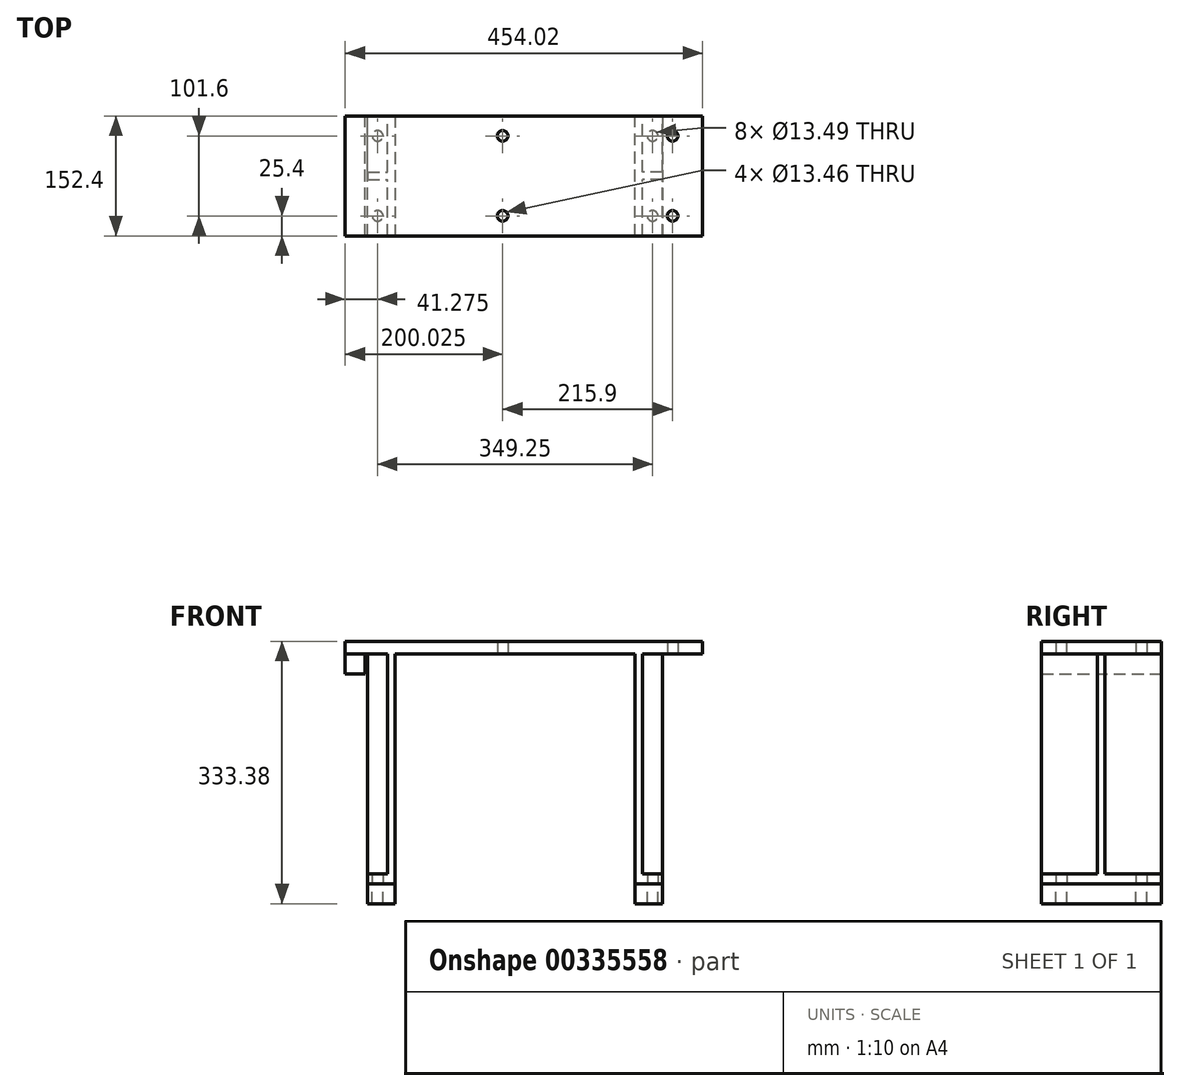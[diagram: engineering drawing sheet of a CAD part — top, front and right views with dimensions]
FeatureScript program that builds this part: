
annotation { "Feature Type Name" : "Feature", "Feature Type Description" : "" }
export const myFeature = defineFeature(function(context is Context, id is Id, definition is map)
    precondition{}
    {
        {
            var Q0;
            Q0=qCreatedBy(makeId("Top.planeOp"),FACE);
            var sketch = newSketch(context, id + "F0", { "sketchPlane" : qUnion([Q0])});
            skLineSegment(sketch, "E0", {"start": v(0, 170.24) * mm, "end": v(0, -171.77) * mm, "construction": true});
            skLineSegment(sketch, "E1", {"start": v(-339.85, 0) * mm, "end": v(353.8, 0) * mm, "construction": true});
            skLineSegment(sketch, "E2.0", {"start": v(-215.9, 170.24) * mm, "end": v(-215.9, -171.77) * mm, "construction": true});
            skLineSegment(sketch, "E3.0", {"start": v(-15.87, 170.24) * mm, "end": v(-15.87, -171.77) * mm, "construction": true});
            skLineSegment(sketch, "E4.0", {"start": v(-339.85, -76.2) * mm, "end": v(353.8, -76.2) * mm, "construction": true});
            skLineSegment(sketch, "E5.bottom", {"start": v(-215.9, -76.2) * mm, "end": v(238.13, -76.2) * mm});
            skLineSegment(sketch, "E5.top", {"start": v(-215.9, 76.2) * mm, "end": v(238.13, 76.2) * mm});
            skLineSegment(sketch, "E5.left", {"start": v(-215.9, -76.2) * mm, "end": v(-215.9, 76.2) * mm});
            skLineSegment(sketch, "E5.right", {"start": v(238.13, -76.2) * mm, "end": v(238.13, 76.2) * mm});
            skLineSegment(sketch, "E6.0", {"start": v(200.03, 170.24) * mm, "end": v(200.03, -171.77) * mm, "construction": true});
            skLineSegment(sketch, "E7.0", {"start": v(-339.85, -50.8) * mm, "end": v(353.8, -50.8) * mm, "construction": true});
            skPoint(sketch, "E8", {"position": v(-15.87, -50.8) * mm});
            skPoint(sketch, "E9", {"position": v(200.03, -50.8) * mm});
            skPoint(sketch, "E10.MirrorP", {"position": v(-15.87, 50.8) * mm});
            skPoint(sketch, "E11.MirrorP", {"position": v(200.03, 50.8) * mm});
            skCircle(sketch, "E12", {"center": v(-15.87, 50.8) * mm, "radius": 6.73 * mm});
            skCircle(sketch, "E13", {"center": v(200.03, 50.8) * mm, "radius": 6.73 * mm});
            skCircle(sketch, "E14", {"center": v(200.03, -50.8) * mm, "radius": 6.73 * mm});
            skCircle(sketch, "E15", {"center": v(-15.87, -50.8) * mm, "radius": 6.73 * mm});
            skSolve(sketch);
        }
        {
            var Q0;
            Q0 = qSketchRegion(id + "F0", true);
            extrude(context, id + "F1", {"entities" : qUnion([Q0]), "depth" : 15.88 * mm});
        }
        {
            var Q0;
            Q0=makeQuery(id+"F1.opExtrude","CAP_FACE",FACE,{"disambiguationData":[OSD([sQuery(id+"F0.wireOp",EDGE,"E5.bottom"),sQuery(id+"F0.wireOp",EDGE,"E5.top"),sQuery(id+"F0.wireOp",EDGE,"E5.left"),sQuery(id+"F0.wireOp",EDGE,"E5.right"),sQuery(id+"F0.wireOp",EDGE,"E12"),sQuery(id+"F0.wireOp",EDGE,"E13"),sQuery(id+"F0.wireOp",EDGE,"E14"),sQuery(id+"F0.wireOp",EDGE,"E15")])],"isStart":true});
            var sketch = newSketch(context, id + "F2", { "sketchPlane" : qUnion([Q0])});
            skLineSegment(sketch, "E16.bottom", {"start": v(-215.9, 76.2) * mm, "end": v(-190.5, 76.2) * mm});
            skLineSegment(sketch, "E16.top", {"start": v(-215.9, -76.2) * mm, "end": v(-190.5, -76.2) * mm});
            skLineSegment(sketch, "E16.left", {"start": v(-215.9, 76.2) * mm, "end": v(-215.9, -76.2) * mm});
            skLineSegment(sketch, "E16.right", {"start": v(-190.5, 76.2) * mm, "end": v(-190.5, -76.2) * mm});
            skSolve(sketch);
        }
        {
            var Q0;
            Q0=makeQuery(id+"F2.imprint","IMPRINT",FACE,{"disambiguationData":[TD([[makeQuery(id+"F2.imprint","IMPRINT",EDGE,{"derivedFrom":sQuery(id+"F2.wireOp",EDGE,"E16.bottom")}),-1.0]])]});
            extrude(context, id + "F3", {"entities" : qUnion([Q0]), "depth" : 25.4 * mm});
        }
        {
            var Q0;
            Q0=makeQuery(id+"F1.opExtrude","CAP_FACE",FACE,{"disambiguationData":[OSD([sQuery(id+"F0.wireOp",EDGE,"E5.bottom"),sQuery(id+"F0.wireOp",EDGE,"E5.top"),sQuery(id+"F0.wireOp",EDGE,"E5.left"),sQuery(id+"F0.wireOp",EDGE,"E5.right"),sQuery(id+"F0.wireOp",EDGE,"E12"),sQuery(id+"F0.wireOp",EDGE,"E13"),sQuery(id+"F0.wireOp",EDGE,"E14"),sQuery(id+"F0.wireOp",EDGE,"E15")])],"isStart":true});
            cPlane(context, id + "F4", {"entities" : qUnion([Q0]), "cplaneType" : CPlaneType.OFFSET, "offset" : 292.1 * mm, "width" : 152.4 * mm, "height" : 152.4 * mm});
        }
        {
            var Q0;
            Q0=qCreatedBy(makeId("Right.planeOp"),FACE);
            cPlane(context, id + "F5", {"entities" : qUnion([Q0]), "cplaneType" : CPlaneType.OFFSET, "offset" : 152.4 * mm, "width" : 152.4 * mm, "height" : 152.4 * mm});
        }
        {
            var Q0;
            Q0=qCreatedBy(id+"F5.planeOp",FACE);
            var sketch = newSketch(context, id + "F6", { "sketchPlane" : qUnion([Q0])});
            skLineSegment(sketch, "E17.0", {"start": v(-76.2, -25.4) * mm, "end": v(76.2, -25.4) * mm, "construction": true});
            skLineSegment(sketch, "E18.0", {"start": v(-76.2, 0) * mm, "end": v(76.2, 0) * mm, "construction": true});
            skLineSegment(sketch, "E19.bottom", {"start": v(76.2, 0) * mm, "end": v(-76.2, 0) * mm});
            skLineSegment(sketch, "E19.top", {"start": v(76.2, -292.1) * mm, "end": v(-76.2, -292.1) * mm});
            skLineSegment(sketch, "E19.left", {"start": v(76.2, 0) * mm, "end": v(76.2, -292.1) * mm});
            skLineSegment(sketch, "E19.right", {"start": v(-76.2, 0) * mm, "end": v(-76.2, -292.1) * mm});
            skSolve(sketch);
        }
        {
            var Q0;
            Q0=makeQuery(id+"F6.imprint","IMPRINT",FACE,{"disambiguationData":[TD([[makeQuery(id+"F6.imprint","IMPRINT",EDGE,{"derivedFrom":sQuery(id+"F6.wireOp",EDGE,"E19.bottom")}),1.0]])]});
            extrude(context, id + "F7", {"entities" : qUnion([Q0]), "depth" : 9.52 * mm});
        }
        {
            var Q0;
            Q0=qCreatedBy(id+"F4.planeOp",FACE);
            var sketch = newSketch(context, id + "F8", { "sketchPlane" : qUnion([Q0])});
            skLineSegment(sketch, "E20.0", {"start": v(161.93, -76.2) * mm, "end": v(161.93, 76.2) * mm, "construction": true});
            skLineSegment(sketch, "E21.0", {"start": v(187.33, -76.2) * mm, "end": v(187.33, 76.2) * mm, "construction": true});
            skLineSegment(sketch, "E22.0", {"start": v(152.4, -76.2) * mm, "end": v(152.4, 76.2) * mm, "construction": true});
            skLineSegment(sketch, "E23.bottom", {"start": v(152.4, 76.2) * mm, "end": v(187.33, 76.2) * mm});
            skLineSegment(sketch, "E23.top", {"start": v(152.4, -76.2) * mm, "end": v(187.33, -76.2) * mm});
            skLineSegment(sketch, "E23.left", {"start": v(152.4, 76.2) * mm, "end": v(152.4, -76.2) * mm});
            skLineSegment(sketch, "E23.right", {"start": v(187.33, 76.2) * mm, "end": v(187.33, -76.2) * mm});
            skSolve(sketch);
        }
        {
            var Q0;
            Q0 = qSketchRegion(id + "F8", true);
            extrude(context, id + "F9", {"entities" : qUnion([Q0]), "operationType" : NewBodyOperationType.ADD, "oppositeDirection" : true, "depth" : 12.7 * mm});
        }
        {
            var Q0;
            Q0=makeQuery(id+"F9.boolean.opBoolean","MERGE",FACE,{"derivedFrom":[makeQuery(id+"F7.opExtrude","SWEPT_FACE",FACE,{"disambiguationData":[OSD([sQuery(id+"F6.wireOp",EDGE,"E19.top")])]}),makeQuery(id+"F9.opExtrude","CAP_FACE",FACE,{"disambiguationData":[OSD([sQuery(id+"F8.wireOp",EDGE,"E23.bottom"),sQuery(id+"F8.wireOp",EDGE,"E23.top"),sQuery(id+"F8.wireOp",EDGE,"E23.left"),sQuery(id+"F8.wireOp",EDGE,"E23.right")])],"isStart":true})]});
            var sketch = newSketch(context, id + "F10", { "sketchPlane" : qUnion([Q0])});
            skLineSegment(sketch, "E24.0", {"start": v(187.33, 76.2) * mm, "end": v(187.33, -76.2) * mm, "construction": true});
            skLineSegment(sketch, "E25.0", {"start": v(174.63, 76.2) * mm, "end": v(174.63, -76.2) * mm, "construction": true});
            skLineSegment(sketch, "E26", {"start": v(261.95, 0) * mm, "end": v(121.14, 0) * mm, "construction": true});
            skPoint(sketch, "E26.startSnap0", {"position": v(187.33, 0) * mm});
            skPoint(sketch, "E26.endSnap0", {"position": v(187.33, 0) * mm});
            skLineSegment(sketch, "E27.0", {"start": v(261.95, 50.8) * mm, "end": v(121.14, 50.8) * mm, "construction": true});
            skPoint(sketch, "E28", {"position": v(174.63, 50.8) * mm});
            skPoint(sketch, "E29.MirrorP", {"position": v(174.63, -50.8) * mm});
            skSolve(sketch);
        }
        {
            var Q0;
            Q0=sQuery(id+"F10.wireOp",VERTEX,"E28");
            var Q1;
            Q1=sQuery(id+"F10.wireOp",VERTEX,"E29.MirrorP");
            var Q2;
            Q2=makeQuery(id+"F7.opExtrude","SWEPT_BODY",BODY,{"disambiguationData":[OSD([sQuery(id+"F6.wireOp",EDGE,"E19.bottom"),sQuery(id+"F6.wireOp",EDGE,"E19.top"),sQuery(id+"F6.wireOp",EDGE,"E19.left"),sQuery(id+"F6.wireOp",EDGE,"E19.right")])]});
            hole(context, id + "F11", {"style" : HoleStyle.SIMPLE, "endStyle" : HoleEndStyle.BLIND, "standardTappedOrClearance" : lookupTablePath({ "standard" : "ANSI", "fit" : "Normal (ASME)", "size" : "1/2", "type" : "Clearance" }), "standardBlindInLast" : lookupTablePath({ "fit" : "Free", "standard" : "ANSI", "size" : "1/2", "type" : "Clearance" }), "holeDiameter" : 13.5 * mm, "holeDepth" : 25.4 * mm, "tappedDepth" : 19.53 * mm, "tapClearance" : 3, "locations" : qUnion([Q0, Q1]), "scope" : qUnion([Q2])});
        }
        {
            var Q0;
            Q0=makeQuery(id+"F7.opExtrude","SWEPT_BODY",BODY,{"disambiguationData":[OSD([sQuery(id+"F6.wireOp",EDGE,"E19.bottom"),sQuery(id+"F6.wireOp",EDGE,"E19.top"),sQuery(id+"F6.wireOp",EDGE,"E19.left"),sQuery(id+"F6.wireOp",EDGE,"E19.right")])]});
            var Q1;
            Q1=qCreatedBy(makeId("Right.planeOp"),FACE);
            mirror(context, id + "F12", {"operationType" : NewBodyOperationType.ADD, "entities" : qUnion([Q0]), "mirrorPlane" : qUnion([Q1])});
        }
        {
            var Q0;
            Q0=makeQuery(id+"F12.opPattern","COPY",FACE,{"derivedFrom":makeQuery(id+"F7.opExtrude","CAP_FACE",FACE,{"disambiguationData":[OSD([sQuery(id+"F6.wireOp",EDGE,"E19.bottom"),sQuery(id+"F6.wireOp",EDGE,"E19.top"),sQuery(id+"F6.wireOp",EDGE,"E19.left"),sQuery(id+"F6.wireOp",EDGE,"E19.right")])],"isStart":false}),"instanceName":"1"});
            var sketch = newSketch(context, id + "F13", { "sketchPlane" : qUnion([Q0])});
            skLineSegment(sketch, "E30", {"start": v(0, 105.63) * mm, "end": v(0, -367.61) * mm, "construction": true});
            skLineSegment(sketch, "E31.0", {"start": v(-4.76, 105.63) * mm, "end": v(-4.76, -367.61) * mm, "construction": true});
            skLineSegment(sketch, "E32.0", {"start": v(76.2, 0) * mm, "end": v(-76.2, 0) * mm, "construction": true});
            skLineSegment(sketch, "E33.0", {"start": v(76.2, -279.4) * mm, "end": v(-76.2, -279.4) * mm, "construction": true});
            skLineSegment(sketch, "E34.bottom", {"start": v(-4.76, -279.4) * mm, "end": v(4.76, -279.4) * mm});
            skLineSegment(sketch, "E34.top", {"start": v(-4.76, 0) * mm, "end": v(4.76, 0) * mm});
            skLineSegment(sketch, "E34.left", {"start": v(-4.76, -279.4) * mm, "end": v(-4.76, 0) * mm});
            skLineSegment(sketch, "E34.right", {"start": v(4.76, -279.4) * mm, "end": v(4.76, 0) * mm});
            skSolve(sketch);
        }
        {
            var Q0;
            Q0 = qSketchRegion(id + "F13", true);
            extrude(context, id + "F14", {"entities" : qUnion([Q0]), "depth" : 25.4 * mm});
        }
        {
            var Q0;
            Q0=makeQuery(id+"F14.opExtrude","SWEPT_BODY",BODY,{"disambiguationData":[OSD([sQuery(id+"F13.wireOp",EDGE,"E34.bottom"),sQuery(id+"F13.wireOp",EDGE,"E34.top"),sQuery(id+"F13.wireOp",EDGE,"E34.left"),sQuery(id+"F13.wireOp",EDGE,"E34.right")])]});
            var Q1;
            Q1=qCreatedBy(makeId("Right.planeOp"),FACE);
            mirror(context, id + "F15", {"operationType" : NewBodyOperationType.ADD, "entities" : qUnion([Q0]), "mirrorPlane" : qUnion([Q1])});
        }
        {
            var Q0;
            Q0=makeQuery(id+"F12.opPattern","COPY",FACE,{"derivedFrom":makeQuery(id+"F9.boolean.opBoolean","MERGE",FACE,{"derivedFrom":[makeQuery(id+"F7.opExtrude","SWEPT_FACE",FACE,{"disambiguationData":[OSD([sQuery(id+"F6.wireOp",EDGE,"E19.top")])]}),makeQuery(id+"F9.opExtrude","CAP_FACE",FACE,{"disambiguationData":[OSD([sQuery(id+"F8.wireOp",EDGE,"E23.bottom"),sQuery(id+"F8.wireOp",EDGE,"E23.top"),sQuery(id+"F8.wireOp",EDGE,"E23.left"),sQuery(id+"F8.wireOp",EDGE,"E23.right")])],"isStart":true})]}),"instanceName":"1"});
            var sketch = newSketch(context, id + "F16", { "sketchPlane" : qUnion([Q0])});
            skLineSegment(sketch, "E35.0.0", {"start": v(-152.4, -76.2) * mm, "end": v(-152.4, 76.2) * mm});
            skLineSegment(sketch, "E35.0.1", {"start": v(-152.4, 76.2) * mm, "end": v(-187.33, 76.2) * mm});
            skLineSegment(sketch, "E35.0.2", {"start": v(-187.33, 76.2) * mm, "end": v(-187.33, -76.2) * mm});
            skLineSegment(sketch, "E35.0.3", {"start": v(-187.33, -76.2) * mm, "end": v(-152.4, -76.2) * mm});
            skCircle(sketch, "E36.0", {"center": v(-174.63, 50.8) * mm, "radius": 6.75 * mm});
            skCircle(sketch, "E37.0", {"center": v(-174.63, -50.8) * mm, "radius": 6.75 * mm});
            skLineSegment(sketch, "E38.0.0", {"start": v(152.4, 76.2) * mm, "end": v(152.4, -76.2) * mm});
            skLineSegment(sketch, "E38.0.1", {"start": v(152.4, -76.2) * mm, "end": v(187.33, -76.2) * mm});
            skLineSegment(sketch, "E38.0.2", {"start": v(187.33, -76.2) * mm, "end": v(187.33, 76.2) * mm});
            skLineSegment(sketch, "E38.0.3", {"start": v(187.33, 76.2) * mm, "end": v(152.4, 76.2) * mm});
            skCircle(sketch, "E39.0", {"center": v(174.63, -50.8) * mm, "radius": 6.75 * mm});
            skCircle(sketch, "E40.0", {"center": v(174.63, 50.8) * mm, "radius": 6.75 * mm});
            skSolve(sketch);
        }
        {
            var Q0;
            Q0 = qSketchRegion(id + "F16", true);
            extrude(context, id + "F17", {"entities" : qUnion([Q0]), "depth" : 25.4 * mm});
        }
    });
